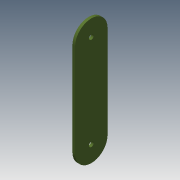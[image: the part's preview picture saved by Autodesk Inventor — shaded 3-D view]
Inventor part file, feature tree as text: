
AUTODESK INVENTOR PART (.ipt)
format: ipt  version: 2013 (Build 170138000, 138)  size: 88,576 bytes
history: native  units: mm
features: extrude x2, sketch x2
ambient origin geometry x8: Origin, YZ Plane, XZ Plane, XY Plane, X Axis, Y Axis, Z Axis, Center Point
bodies: Solid1 (feature_tree)
feature tree (4):
  extrude  "Extrusion1"  Depth=120.0mm
  extrude  "Extrusion2"  Depth=42.0mm
  sketch  "Sketch1"  dims[d0=42.0mm d1=120.0mm]
  sketch  "Sketch2"  dims[d2=42.0mm d3=42.0mm d4=3.4mm d5=0.0mm d6=6.0mm d7=6.0mm d8=3.4mm d9=0.0mm]
